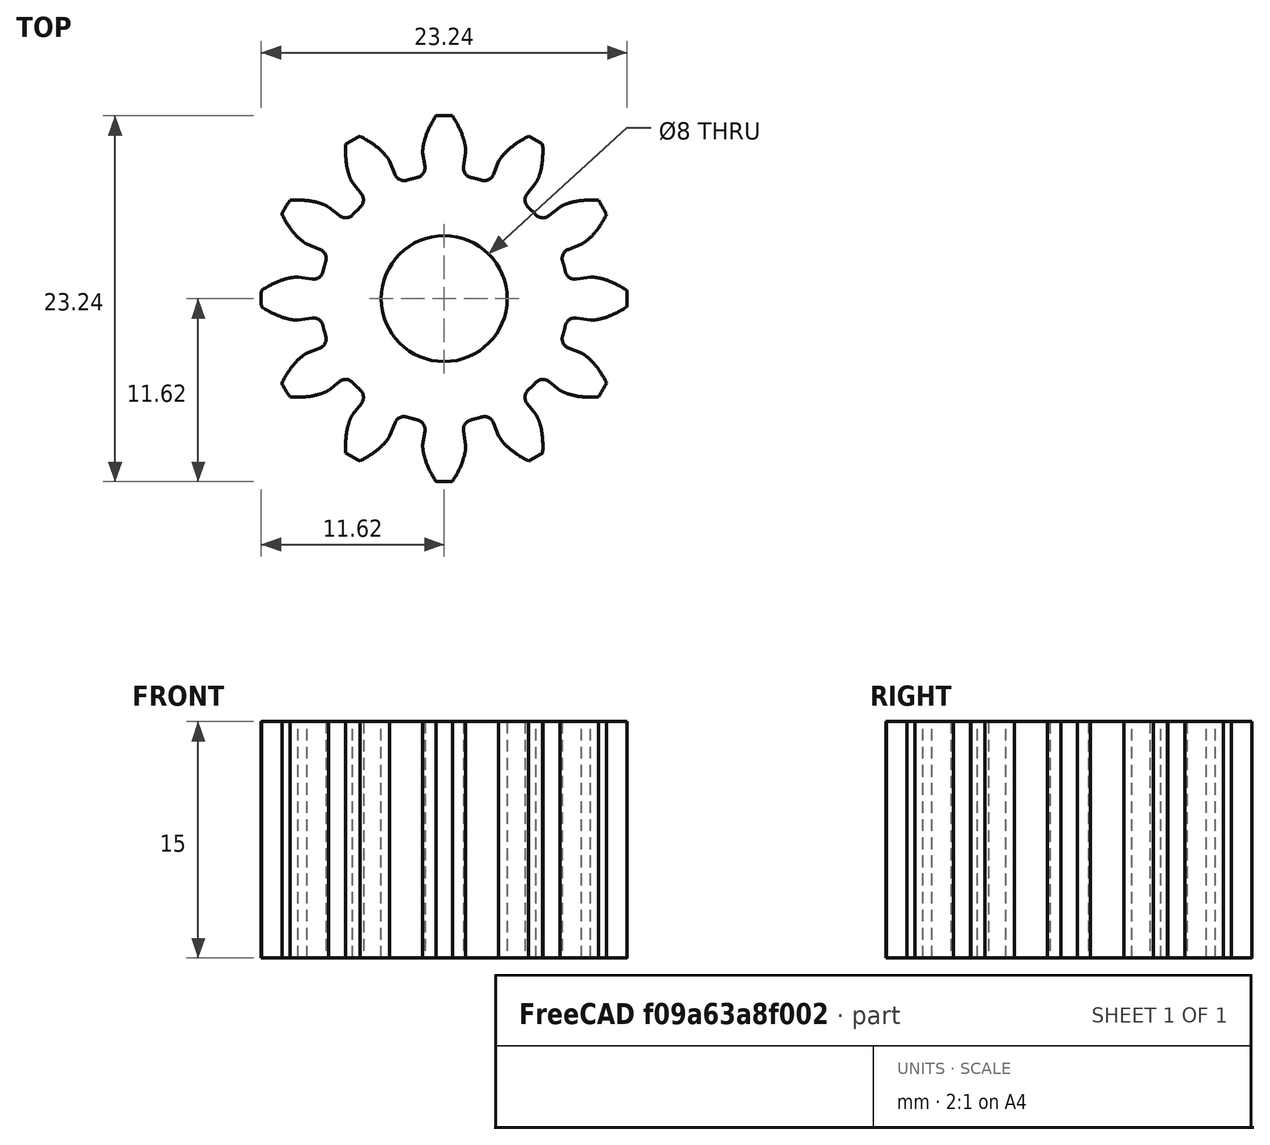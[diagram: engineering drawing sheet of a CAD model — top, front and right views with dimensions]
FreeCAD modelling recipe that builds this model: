
FCSTD DOCUMENT  (FreeCAD 0.18R4 (GitTag))
Label: Engranje 15mm 12 dientes 1.66
License: All rights reserved
LicenseURL: http://en.wikipedia.org/wiki/All_rights_reserved
objects: Part::Part2DObjectPython×1, PartDesign::Pad×1, Sketcher::SketchObject×1, PartDesign::Pocket×1, PartDesign::Body×1
note: 7 computed .brp shape members not serialized (recipe doc carries the construction recipe); baked Part::Feature solids carry a one-line shape summary decoded from their .brp

FEATURE [Part::Part2DObjectPython] InvoluteGear  # Draft 2D object (typed FeaturePython)
  ExternalGear = true
  HighPrecision = true
  Modules = 1.66
  NumberOfTeeth = 12
  PressureAngle = 20
FEATURE [PartDesign::Pad] Pad
  Length = 15
  Length2 = 100
  Profile = -> InvoluteGear
  Type = 0
FEATURE [Sketcher::SketchObject] Sketch
  MapMode = 5
  Placement = pos=(0,0,15) rot=(0,0,1;0rad)
  Support = -> [Pad]
  expr: Constraints[0] = 8 / 2
  sketch-geometry (1):
    g0: Circle CenterX=0 CenterY=0 CenterZ=0 NormalX=0 NormalY=0 NormalZ=1 AngleXU=0 Radius=4
  constraints (1):
    c: Radius(g0) = 4
FEATURE [PartDesign::Pocket] Pocket
  BaseFeature = -> Pad
  Length = 15
  Length2 = 100
  Profile = -> Sketch
  Type = 0
FEATURE [PartDesign::Body] Body
  Group = -> [InvoluteGear,Pad,Sketch,Pocket]
  Origin = -> Origin
  Tip = -> Pocket
